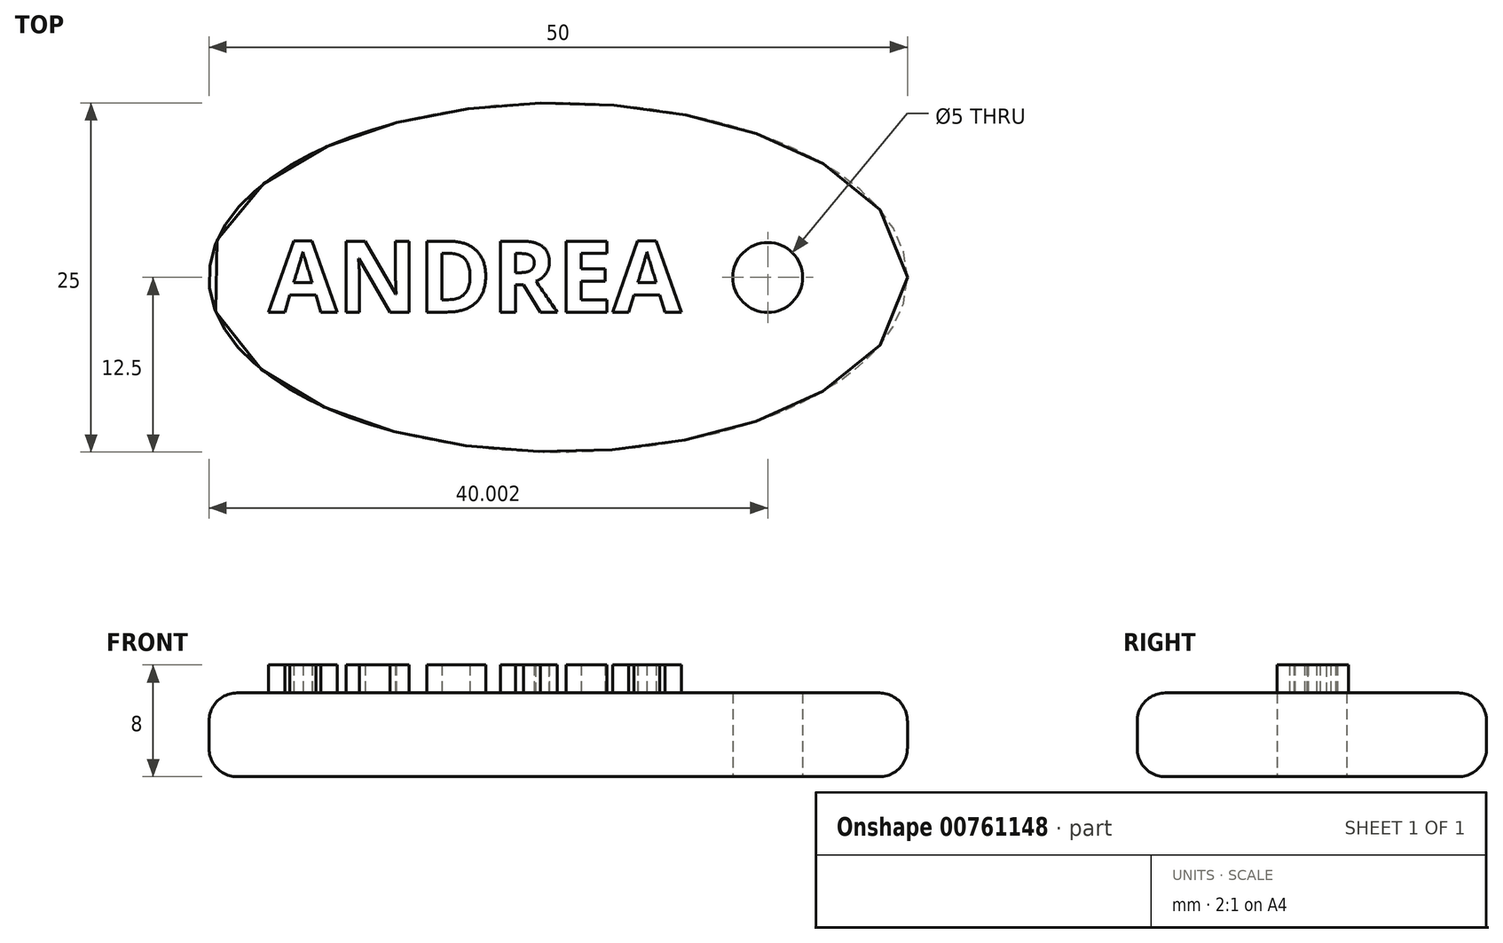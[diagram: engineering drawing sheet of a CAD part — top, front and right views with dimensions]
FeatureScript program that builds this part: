
annotation { "Feature Type Name" : "Feature", "Feature Type Description" : "" }
export const myFeature = defineFeature(function(context is Context, id is Id, definition is map)
    precondition{}
    {
        {
            var Q0;
            Q0=qCreatedBy(makeId("Top.planeOp"),FACE);
            var sketch = newSketch(context, id + "F0", { "sketchPlane" : qUnion([Q0])});
            skEllipse(sketch, "E0", {"center": v(3.01, 0) * mm, "majorRadius": 25 * mm, "minorRadius": 12.5 * mm, "majorAxis": v(1, 0)});
            skLineSegment(sketch, "E1", {"start": v(28.01, 0) * mm, "end": v(18.01, 0) * mm});
            skCircle(sketch, "E2", {"center": v(18.01, 0) * mm, "radius": 2.5 * mm});
            skSolve(sketch);
        }
        {
            var Q0;
            Q0 = qSketchRegion(id + "F0", true);
            extrude(context, id + "F1", {"entities" : qUnion([Q0]), "depth" : 6 * mm, "offsetDistance" : 25 * mm});
        }
        {
            var Q0;
            Q0=makeQuery(id+"F1.opExtrude","CAP_FACE",FACE,{"disambiguationData":[OSD([sQuery(id+"F0.wireOp",EDGE,"E0"),sQuery(id+"F0.wireOp",EDGE,"E2")])],"isStart":false});
            var sketch = newSketch(context, id + "F2", { "sketchPlane" : qUnion([Q0])});
            skText(sketch, "E3", { "text": "ANDREA", "fontName": "OpenSans-Bold.ttf"});
            const initialGuessF2  = {"E3": [-0.01772, -0.00248, 1, 0, 0.00512]};
            skSetInitialGuess(sketch, initialGuessF2);
            skSolve(sketch);
        }
        {
            var Q0;
            Q0 = qSketchRegion(id + "F2", true);
            extrude(context, id + "F3", {"entities" : qUnion([Q0]), "operationType" : NewBodyOperationType.ADD, "depth" : 2 * mm, "offsetDistance" : 25 * mm});
        }
        {
            var Q0;
            Q0=makeQuery(id+"F1.opExtrude","CAP_EDGE",EDGE,{"disambiguationData":[OSD([sQuery(id+"F0.wireOp",EDGE,"E0")])],"isStart":false});
            var Q1;
            Q1=makeQuery(id+"F1.opExtrude","CAP_EDGE",EDGE,{"disambiguationData":[OSD([sQuery(id+"F0.wireOp",EDGE,"E0")])],"isStart":true});
            fillet(context, id + "F4", {"entities" : qUnion([Q0, Q1]), "radius" : 2 * mm, "tangentPropagation" : true, "allowEdgeOverflow" : false});
        }
    });
